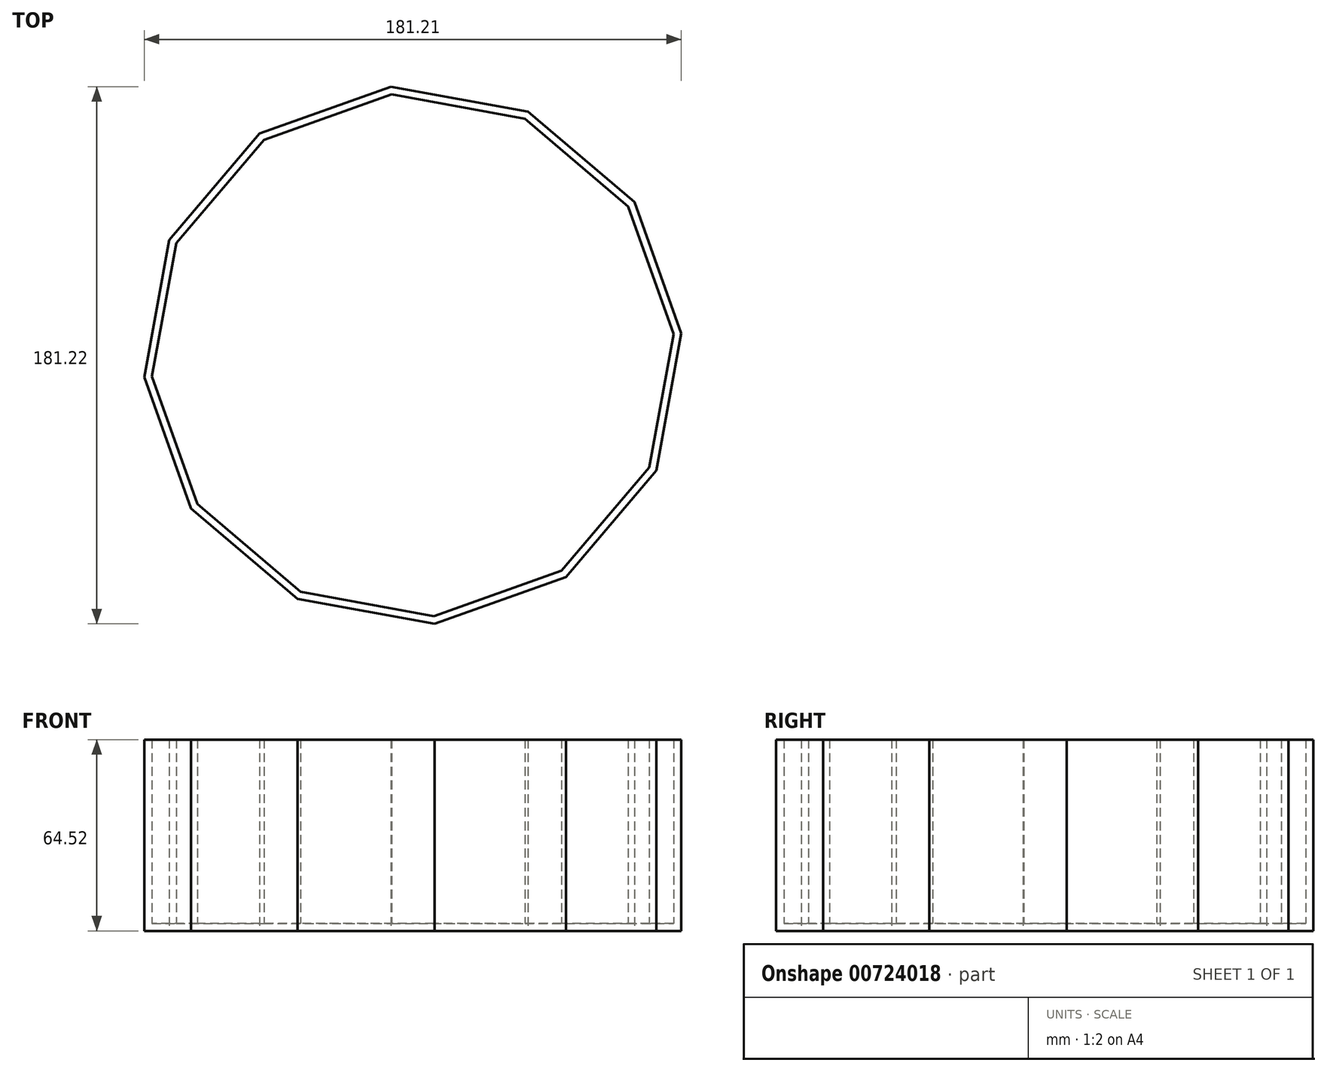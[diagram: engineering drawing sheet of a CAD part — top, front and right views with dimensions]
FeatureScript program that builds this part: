
annotation { "Feature Type Name" : "Feature", "Feature Type Description" : "" }
export const myFeature = defineFeature(function(context is Context, id is Id, definition is map)
    precondition{}
    {
        {
            var Q0;
            Q0=qCreatedBy(makeId("Top.planeOp"),FACE);
            var sketch = newSketch(context, id + "F0", { "sketchPlane" : qUnion([Q0])});
            skCircle(sketch, "E0.cCircle", {"center": v(15.8, -50.29) * mm, "radius": 87.8 * mm, "construction": true});
            skLineSegment(sketch, "E0.0", {"start": v(-35.88, 24.5) * mm, "end": v(8.43, 40.32) * mm});
            skLineSegment(sketch, "E0.1", {"start": v(8.43, 40.32) * mm, "end": v(54.73, 31.87) * mm});
            skLineSegment(sketch, "E0.2", {"start": v(54.73, 31.87) * mm, "end": v(90.59, 1.4) * mm});
            skLineSegment(sketch, "E0.3", {"start": v(90.59, 1.4) * mm, "end": v(106.41, -42.92) * mm});
            skLineSegment(sketch, "E0.4", {"start": v(106.41, -42.92) * mm, "end": v(97.96, -89.2) * mm});
            skLineSegment(sketch, "E0.5", {"start": v(97.96, -89.2) * mm, "end": v(67.5, -125.07) * mm});
            skLineSegment(sketch, "E0.6", {"start": v(67.5, -125.07) * mm, "end": v(23.18, -140.9) * mm});
            skLineSegment(sketch, "E0.7", {"start": v(23.18, -140.9) * mm, "end": v(-23.11, -132.44) * mm});
            skLineSegment(sketch, "E0.8", {"start": v(-23.11, -132.44) * mm, "end": v(-58.98, -101.98) * mm});
            skLineSegment(sketch, "E0.9", {"start": v(-58.98, -101.98) * mm, "end": v(-74.8, -57.66) * mm});
            skLineSegment(sketch, "E0.10", {"start": v(-74.8, -57.66) * mm, "end": v(-66.35, -11.37) * mm});
            skLineSegment(sketch, "E0.11", {"start": v(-66.35, -11.37) * mm, "end": v(-35.88, 24.5) * mm});
            skPoint(sketch, "E0.0.midPoint", {"position": v(-13.72, 32.4) * mm});
            skSolve(sketch);
        }
        {
            var Q0;
            Q0=makeQuery(id+"F0.imprint","IMPRINT",FACE,{"disambiguationData":[TD([[makeQuery(id+"F0.imprint","IMPRINT",EDGE,{"derivedFrom":sQuery(id+"F0.wireOp",EDGE,"E0.0")}),-1.0]])]});
            extrude(context, id + "F1", {"entities" : qUnion([Q0]), "depth" : 64.52 * mm, "offsetDistance" : 25.4 * mm});
        }
        {
            var Q0;
            Q0=makeQuery(id+"F1.opExtrude","CAP_FACE",FACE,{"disambiguationData":[OSD([sQuery(id+"F0.wireOp",EDGE,"E0.0"),sQuery(id+"F0.wireOp",EDGE,"E0.1"),sQuery(id+"F0.wireOp",EDGE,"E0.2"),sQuery(id+"F0.wireOp",EDGE,"E0.3"),sQuery(id+"F0.wireOp",EDGE,"E0.4"),sQuery(id+"F0.wireOp",EDGE,"E0.5"),sQuery(id+"F0.wireOp",EDGE,"E0.6"),sQuery(id+"F0.wireOp",EDGE,"E0.7"),sQuery(id+"F0.wireOp",EDGE,"E0.8"),sQuery(id+"F0.wireOp",EDGE,"E0.9"),sQuery(id+"F0.wireOp",EDGE,"E0.10"),sQuery(id+"F0.wireOp",EDGE,"E0.11")])],"isStart":false});
            shell(context, id + "F2", {"entities" : qUnion([Q0]), "thickness" : 2.54 * mm});
        }
    });
